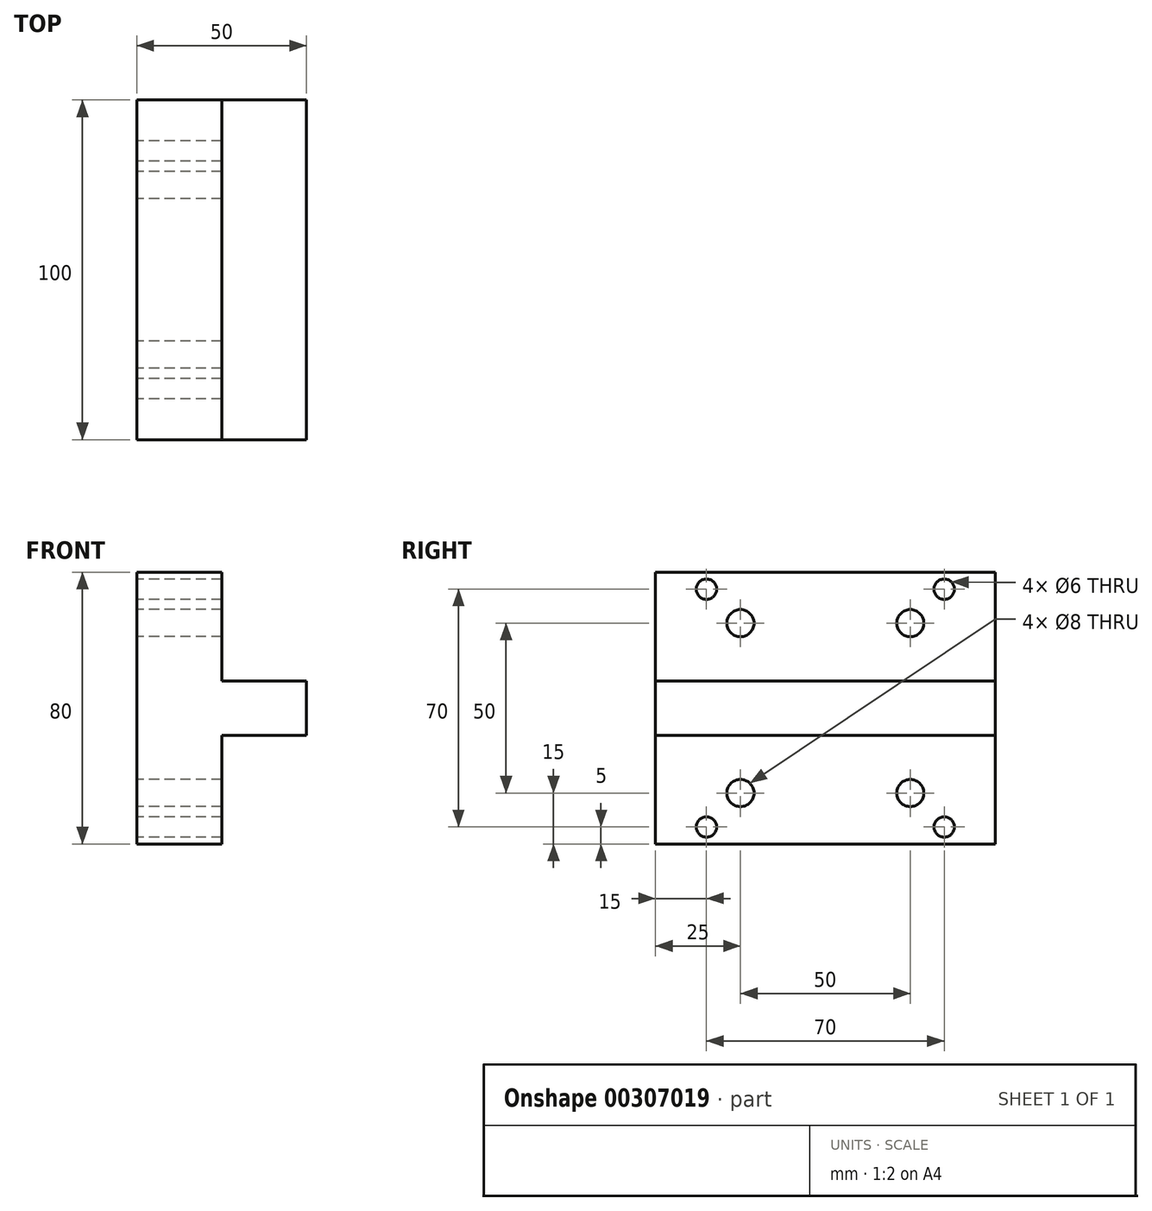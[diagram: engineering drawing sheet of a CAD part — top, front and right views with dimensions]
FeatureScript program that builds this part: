
annotation { "Feature Type Name" : "Feature", "Feature Type Description" : "" }
export const myFeature = defineFeature(function(context is Context, id is Id, definition is map)
    precondition{}
    {
        {
            var Q0;
            Q0=qCreatedBy(makeId("Front.planeOp"),FACE);
            var sketch = newSketch(context, id + "F0", { "sketchPlane" : qUnion([Q0])});
            skLineSegment(sketch, "E0.left", {"start": v(5.19, 0) * mm, "end": v(5.19, -40) * mm});
            skLineSegment(sketch, "E0.right", {"start": v(55.19, 8) * mm, "end": v(55.19, -8) * mm});
            skLineSegment(sketch, "E1", {"start": v(5.19, 0) * mm, "end": v(5.19, 0) * mm});
            skLineSegment(sketch, "E2", {"start": v(5.19, 0) * mm, "end": v(5.19, 40) * mm});
            skLineSegment(sketch, "E3", {"start": v(55.19, 8) * mm, "end": v(30.19, 8) * mm});
            skLineSegment(sketch, "E4", {"start": v(30.19, 8) * mm, "end": v(30.19, 40) * mm});
            skLineSegment(sketch, "E5", {"start": v(30.19, 40) * mm, "end": v(5.19, 40) * mm});
            skLineSegment(sketch, "E6", {"start": v(5.19, -40) * mm, "end": v(30.19, -40) * mm});
            skLineSegment(sketch, "E7", {"start": v(30.19, -40) * mm, "end": v(30.19, -8) * mm});
            skLineSegment(sketch, "E8", {"start": v(30.19, -8) * mm, "end": v(55.19, -8) * mm});
            skSolve(sketch);
        }
        {
            var Q0;
            Q0=qSketchRegion(id+"F0",true);
            extrude(context, id + "F1", {"entities" : qUnion([Q0]), "depth" : 100 * mm});
        }
        {
            var Q0;
            Q0=makeQuery(id+"F1.opExtrude","SWEPT_FACE",FACE,{"disambiguationData":[OSD([sQuery(id+"F0.wireOp",EDGE,"E2")])]});
            var sketch = newSketch(context, id + "F2", { "sketchPlane" : qUnion([Q0])});
            skCircle(sketch, "E9", {"center": v(25, 25) * mm, "radius": 4 * mm});
            skCircle(sketch, "E10", {"center": v(75, 25) * mm, "radius": 4 * mm});
            skCircle(sketch, "E11", {"center": v(25, -25) * mm, "radius": 4 * mm});
            skCircle(sketch, "E12", {"center": v(75, -25) * mm, "radius": 4 * mm});
            skCircle(sketch, "E13", {"center": v(15, 35) * mm, "radius": 3 * mm});
            skCircle(sketch, "E14", {"center": v(85, 35) * mm, "radius": 3 * mm});
            skCircle(sketch, "E15.MirrorC", {"center": v(15, -35) * mm, "radius": 3 * mm});
            skCircle(sketch, "E16.MirrorC", {"center": v(85, -35) * mm, "radius": 3 * mm});
            skSolve(sketch);
        }
        {
            var Q0;
            Q0=qSketchRegion(id+"F2",true);
            extrude(context, id + "F3", {"entities" : qUnion([Q0]), "operationType" : NewBodyOperationType.REMOVE, "oppositeDirection" : true, "depth" : 100 * mm, "symmetric" : true});
        }
    });
